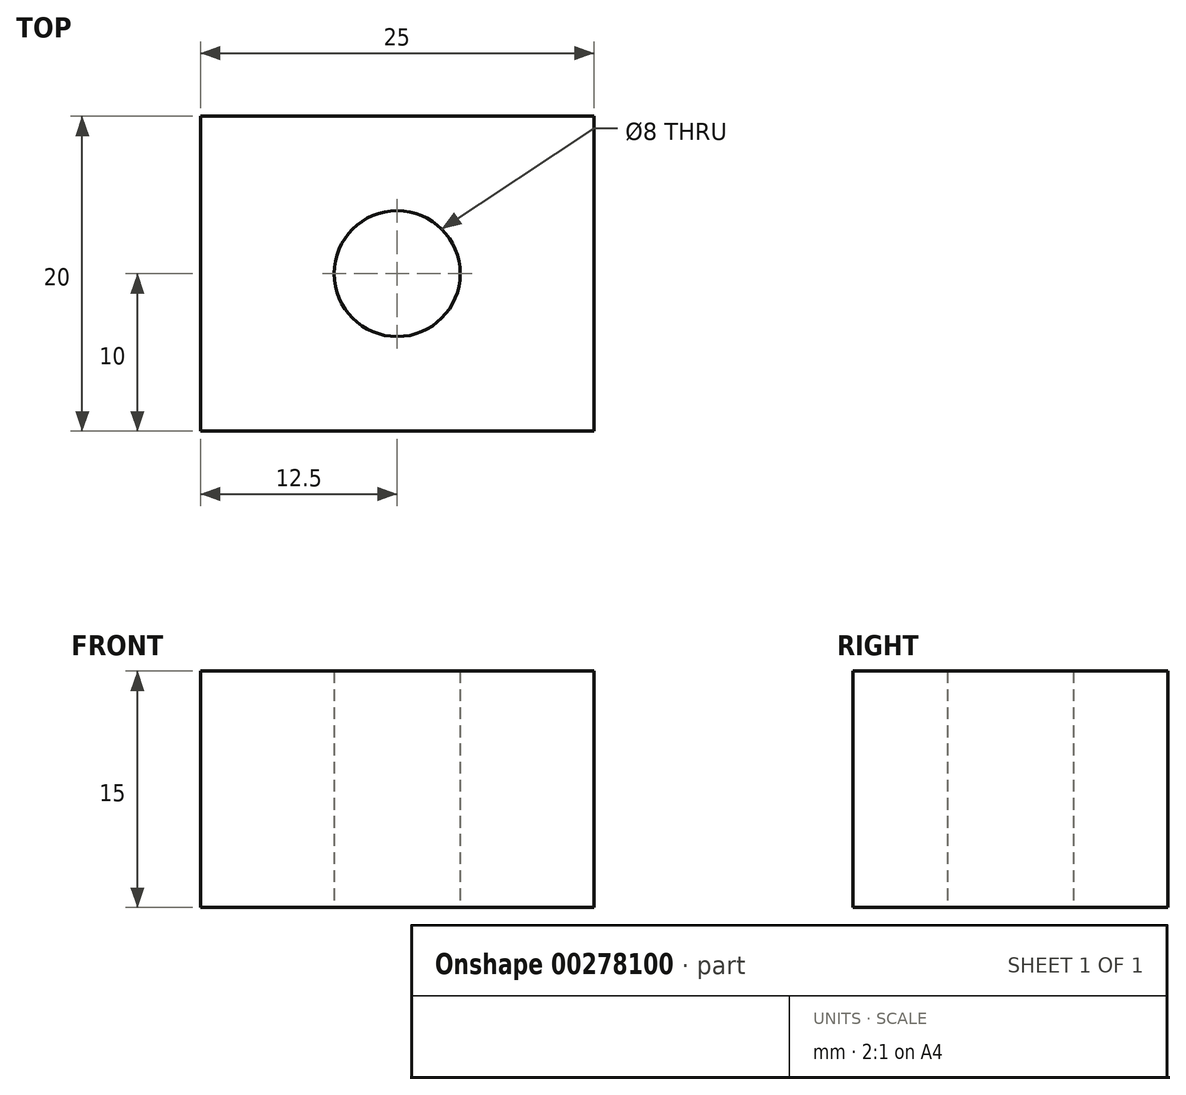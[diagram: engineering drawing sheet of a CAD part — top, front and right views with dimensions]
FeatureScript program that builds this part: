
annotation { "Feature Type Name" : "Feature", "Feature Type Description" : "" }
export const myFeature = defineFeature(function(context is Context, id is Id, definition is map)
    precondition{}
    {
        {
            var Q0;
            Q0=qCreatedBy(makeId("Top.planeOp"),FACE);
            var sketch = newSketch(context, id + "F0", { "sketchPlane" : qUnion([Q0])});
            skLineSegment(sketch, "E0.bottom", {"start": v(0, 0) * mm, "end": v(-25, 0) * mm});
            skLineSegment(sketch, "E0.top", {"start": v(0, 20) * mm, "end": v(-25, 20) * mm});
            skLineSegment(sketch, "E0.left", {"start": v(0, 0) * mm, "end": v(0, 20) * mm});
            skLineSegment(sketch, "E0.right", {"start": v(-25, 0) * mm, "end": v(-25, 20) * mm});
            skCircle(sketch, "E1", {"center": v(-12.5, 10) * mm, "radius": 4 * mm});
            skLineSegment(sketch, "E2", {"start": v(-12.5, 10) * mm, "end": v(-12.5, 20) * mm, "construction": true});
            skLineSegment(sketch, "E3", {"start": v(-12.5, 10) * mm, "end": v(0, 10) * mm, "construction": true});
            skSolve(sketch);
        }
        {
            var Q0;
            Q0=makeQuery(id+"F0.imprint","IMPRINT",FACE,{"disambiguationData":[TD([[makeQuery(id+"F0.imprint","IMPRINT",EDGE,{"derivedFrom":sQuery(id+"F0.wireOp",EDGE,"E0.bottom")}),-1.0]])]});
            extrude(context, id + "F1", {"entities" : qUnion([Q0]), "depth" : 15 * mm});
        }
    });
